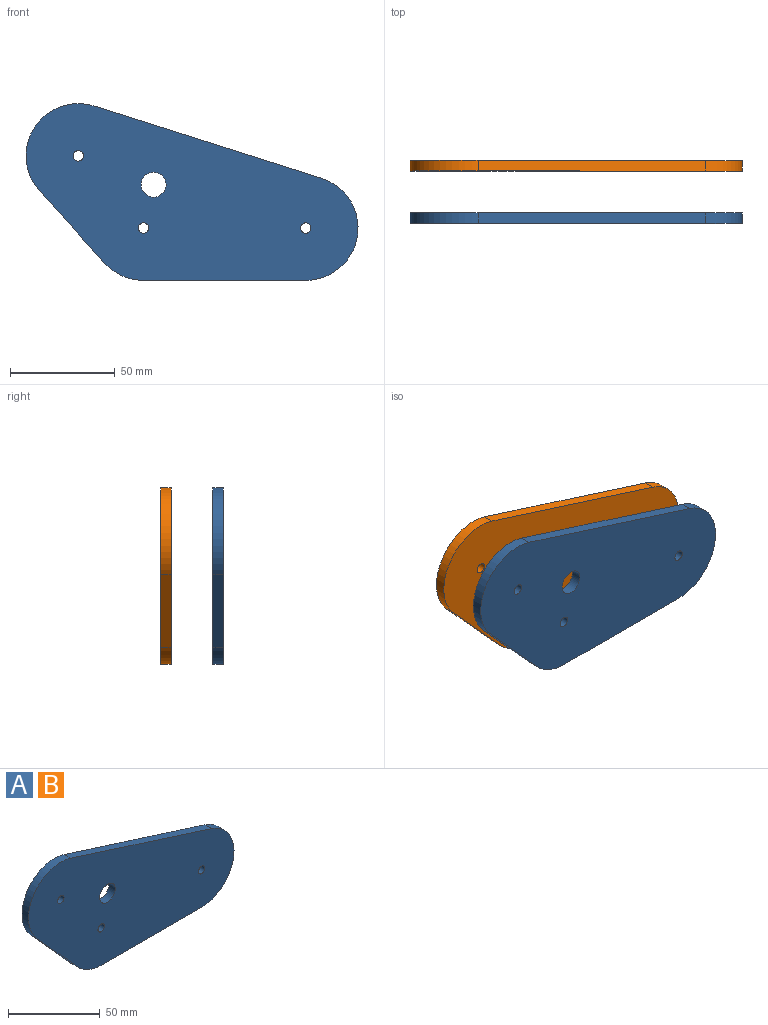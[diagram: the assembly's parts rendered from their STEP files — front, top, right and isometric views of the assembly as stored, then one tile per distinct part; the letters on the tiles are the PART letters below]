
ASSEMBLY  parts=2 mates=1
PART A: 12 faces, bbox 158.8x5x84.6 mm
  f0: plane 34.57x31.2mm, normal (-0.74,0,-0.67), area 232.8mm2, adj f3,f4,f5,f6
  f1: plane 77.61x5mm, normal (0,0,-1), area 388.1mm2, adj f3,f4,f6,f7
  f2: plane 108.82x34.57mm, normal (0.3,0,0.95), area 570.9mm2, adj f3,f4,f5,f7
  f3: plane 158.82x84.57mm, normal (0,-1,0), area 9091.9mm2, adj f0,f1,f2,f5,f6,f7,f8,f9
  f4: plane 158.82x84.57mm, normal (0,1,0), area 9091.9mm2, adj f0,f1,f2,f5,f6,f7,f8,f9
  f5: cylinder r=25mm len=41.75mm, axis (0,1,0), area 326.6mm2, adj f0,f2,f3,f4
  f6: cylinder r=25mm len=18.56mm, axis (0,1,0), area 104.6mm2, adj f0,f1,f3,f4
  f7: cylinder r=25mm len=48.83mm, axis (0,1,0), area 354.3mm2, adj f1,f2,f3,f4
  f8: cylinder r=2.5mm len=5mm, axis (0,-1,0), area 78.5mm2, adj f3,f4
  f9: cylinder r=2.5mm len=5mm, axis (0,-1,0), area 78.5mm2, adj f3,f4
  f10: cylinder r=2.5mm len=5mm, axis (0,-1,0), area 78.5mm2, adj f3,f4
  f11: cylinder r=6mm len=12mm, axis (0,-1,0), area 188.5mm2, adj f3,f4
PART B: same geometry as A
PLACE A t=(-11.14,34.53,11.97)mm
PLACE B t=(-11.14,59.53,11.97)mm
MATE fastened A.f7 <-> B.f7  axis (0,1,0) through (77.58,34.53,36.97)mm
